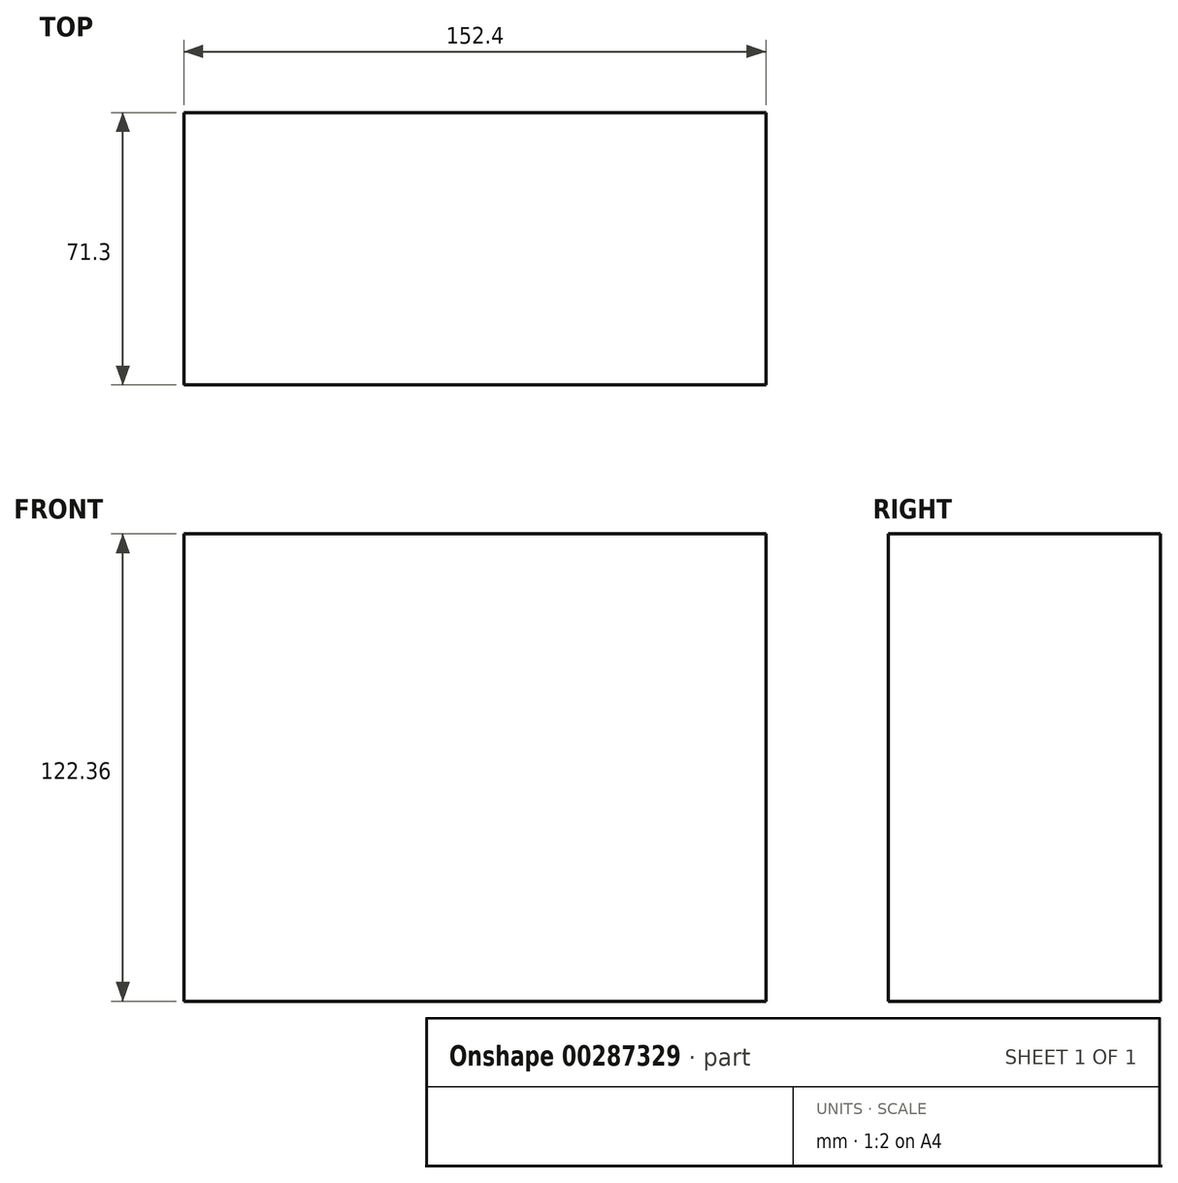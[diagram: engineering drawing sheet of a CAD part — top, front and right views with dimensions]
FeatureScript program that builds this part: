
annotation { "Feature Type Name" : "Feature", "Feature Type Description" : "" }
export const myFeature = defineFeature(function(context is Context, id is Id, definition is map)
    precondition{}
    {
        {
            var Q0;
            Q0=qCreatedBy(makeId("Right.planeOp"),FACE);
            var sketch = newSketch(context, id + "F0", { "sketchPlane" : qUnion([Q0])});
            skLineSegment(sketch, "E0.bottom", {"start": v(0, 0) * mm, "end": v(71.3, 0) * mm});
            skLineSegment(sketch, "E0.top", {"start": v(0, 122.36) * mm, "end": v(71.3, 122.36) * mm});
            skLineSegment(sketch, "E0.left", {"start": v(0, 0) * mm, "end": v(0, 122.36) * mm});
            skLineSegment(sketch, "E0.right", {"start": v(71.3, 0) * mm, "end": v(71.3, 122.36) * mm});
            skSolve(sketch);
        }
        {
            var Q0;
            Q0=makeQuery(id+"F0.imprint","IMPRINT",FACE,{"disambiguationData":[TD([[makeQuery(id+"F0.imprint","IMPRINT",EDGE,{"derivedFrom":sQuery(id+"F0.wireOp",EDGE,"E0.bottom")}),1.0]])]});
            extrude(context, id + "F1", {"entities" : qUnion([Q0]), "depth" : 152.4 * mm});
        }
    });
